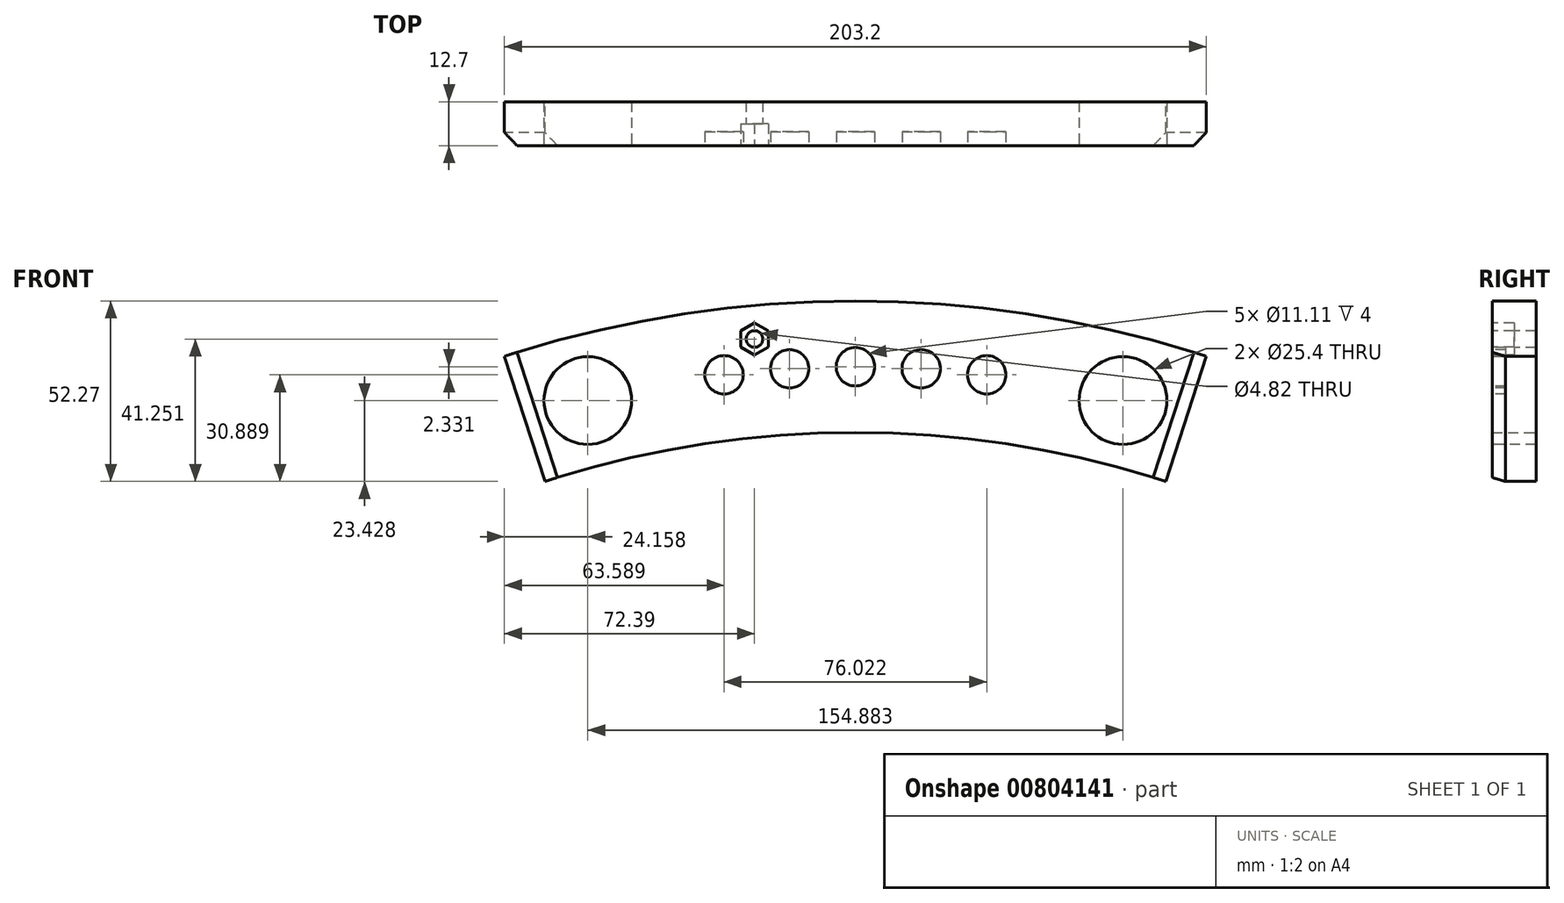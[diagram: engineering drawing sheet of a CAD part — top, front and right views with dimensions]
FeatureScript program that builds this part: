
annotation { "Feature Type Name" : "Feature", "Feature Type Description" : "" }
export const myFeature = defineFeature(function(context is Context, id is Id, definition is map)
    precondition{}
    {
        {
            var Q0;
            Q0=qCreatedBy(makeId("Front.planeOp"),FACE);
            var sketch = newSketch(context, id + "F0", { "sketchPlane" : qUnion([Q0])});
            skLineSegment(sketch, "E0", {"start": v(-101.6, 0) * mm, "end": v(101.6, 0) * mm, "construction": true});
            skArc(sketch, "E1", {"start": v(101.6, 0) * mm, "mid": v(0, 16.02) * mm, "end": v(-101.6, 0) * mm});
            skArc(sketch, "E2.0", {"start": v(89.88, -36.25) * mm, "mid": v(0, -22.08) * mm, "end": v(-89.88, -36.25) * mm});
            skLineSegment(sketch, "E3", {"start": v(-101.6, 0) * mm, "end": v(-89.88, -36.25) * mm});
            skLineSegment(sketch, "E4", {"start": v(101.6, 0) * mm, "end": v(89.88, -36.25) * mm});
            skSolve(sketch);
        }
        {
            var Q0;
            Q0 = qSketchRegion(id + "F0", true);
            extrude(context, id + "F1", {"entities" : qUnion([Q0]), "depth" : 12.7 * mm, "offsetDistance" : 25.4 * mm});
        }
        {
            var Q0;
            Q0=makeQuery(id+"F1.opExtrude","CAP_FACE",FACE,{"disambiguationData":[OSD([sQuery(id+"F0.wireOp",EDGE,"E1"),sQuery(id+"F0.wireOp",EDGE,"E2.0"),sQuery(id+"F0.wireOp",EDGE,"E3"),sQuery(id+"F0.wireOp",EDGE,"E4")])],"isStart":false});
            var sketch = newSketch(context, id + "F2", { "sketchPlane" : qUnion([Q0])});
            skLineSegment(sketch, "E5", {"start": v(0, 16.02) * mm, "end": v(0, -22.08) * mm, "construction": true});
            skPoint(sketch, "E6", {"position": v(0, -3.03) * mm});
            skArc(sketch, "E7", {"start": v(95.74, -18.13) * mm, "mid": v(0, -3.03) * mm, "end": v(-95.74, -18.13) * mm, "construction": true});
            skCircle(sketch, "E8", {"center": v(0, -3.03) * mm, "radius": 5.56 * mm});
            skCircle(sketch, "E9", {"center": v(19.04, -3.61) * mm, "radius": 5.56 * mm});
            skCircle(sketch, "E10", {"center": v(38.01, -5.36) * mm, "radius": 5.56 * mm});
            skLineSegment(sketch, "E11", {"start": v(0, -3.03) * mm, "end": v(19.04, -3.61) * mm, "construction": true});
            skLineSegment(sketch, "E12", {"start": v(19.04, -3.61) * mm, "end": v(38.01, -5.36) * mm, "construction": true});
            skCircle(sketch, "E13.MirrorC", {"center": v(-38.01, -5.36) * mm, "radius": 5.56 * mm});
            skCircle(sketch, "E14.MirrorC", {"center": v(-19.04, -3.61) * mm, "radius": 5.56 * mm});
            skSolve(sketch);
        }
        {
            var Q0;
            Q0 = qSketchRegion(id + "F2", true);
            extrude(context, id + "F3", {"entities" : qUnion([Q0]), "operationType" : NewBodyOperationType.REMOVE, "oppositeDirection" : true, "depth" : 4 * mm, "offsetDistance" : 25.4 * mm});
        }
        {
            var Q0;
            Q0=makeQuery(id+"F1.opExtrude","CAP_FACE",FACE,{"disambiguationData":[OSD([sQuery(id+"F0.wireOp",EDGE,"E1"),sQuery(id+"F0.wireOp",EDGE,"E2.0"),sQuery(id+"F0.wireOp",EDGE,"E3"),sQuery(id+"F0.wireOp",EDGE,"E4")])],"isStart":false});
            var sketch = newSketch(context, id + "F4", { "sketchPlane" : qUnion([Q0])});
            skLineSegment(sketch, "E15", {"start": v(0, 16.02) * mm, "end": v(0, -22.08) * mm, "construction": true});
            skPoint(sketch, "E16", {"position": v(0, -3.03) * mm});
            skArc(sketch, "E17", {"start": v(95.74, -18.13) * mm, "mid": v(0, -3.03) * mm, "end": v(-95.74, -18.13) * mm, "construction": true});
            skCircle(sketch, "E18", {"center": v(77.44, -12.82) * mm, "radius": 12.7 * mm});
            skCircle(sketch, "E19", {"center": v(-77.44, -12.82) * mm, "radius": 12.7 * mm});
            skLineSegment(sketch, "E20", {"start": v(77.44, -12.82) * mm, "end": v(95.74, -18.13) * mm, "construction": true});
            skLineSegment(sketch, "E21", {"start": v(-95.74, -18.13) * mm, "end": v(-77.44, -12.82) * mm, "construction": true});
            skSolve(sketch);
        }
        {
            var Q0;
            Q0 = qSketchRegion(id + "F4", true);
            extrude(context, id + "F5", {"entities" : qUnion([Q0]), "operationType" : NewBodyOperationType.REMOVE, "endBound" : BoundingType.THROUGH_ALL, "oppositeDirection" : true, "depth" : 25.4 * mm, "offsetDistance" : 25.4 * mm});
        }
        {
            var Q0;
            Q0=makeQuery(id+"F1.opExtrude","CAP_EDGE",EDGE,{"disambiguationData":[OSD([sQuery(id+"F0.wireOp",EDGE,"E3")])],"isStart":false});
            var Q1;
            Q1=makeQuery(id+"F1.opExtrude","CAP_EDGE",EDGE,{"disambiguationData":[OSD([sQuery(id+"F0.wireOp",EDGE,"E4")])],"isStart":false});
            chamfer(context, id + "F6", {"entities" : qUnion([Q0, Q1]), "width" : 3.8 * mm, "tangentPropagation" : true});
        }
        {
            var Q0;
            Q0=makeQuery(id+"F1.opExtrude","CAP_FACE",FACE,{"disambiguationData":[OSD([sQuery(id+"F0.wireOp",EDGE,"E1"),sQuery(id+"F0.wireOp",EDGE,"E2.0"),sQuery(id+"F0.wireOp",EDGE,"E3"),sQuery(id+"F0.wireOp",EDGE,"E4")])],"isStart":false});
            var sketch = newSketch(context, id + "F7", { "sketchPlane" : qUnion([Q0])});
            skCircle(sketch, "E22.cCircle", {"center": v(-29.21, 5) * mm, "radius": 4 * mm, "construction": true});
            skLineSegment(sketch, "E22.0", {"start": v(-25.2, 2.7) * mm, "end": v(-29.2, 0.38) * mm});
            skLineSegment(sketch, "E22.1", {"start": v(-29.2, 0.38) * mm, "end": v(-33.2, 2.7) * mm});
            skLineSegment(sketch, "E22.2", {"start": v(-33.2, 2.7) * mm, "end": v(-33.2, 7.31) * mm});
            skLineSegment(sketch, "E22.3", {"start": v(-33.2, 7.31) * mm, "end": v(-29.21, 9.62) * mm});
            skLineSegment(sketch, "E22.4", {"start": v(-29.2, 9.62) * mm, "end": v(-25.2, 7.31) * mm});
            skLineSegment(sketch, "E22.5", {"start": v(-25.21, 7.31) * mm, "end": v(-25.21, 2.7) * mm});
            skPoint(sketch, "E22.0.midPoint", {"position": v(-27.21, 1.54) * mm});
            skSolve(sketch);
        }
        {
            var Q0;
            Q0 = qSketchRegion(id + "F7", true);
            extrude(context, id + "F8", {"entities" : qUnion([Q0]), "operationType" : NewBodyOperationType.REMOVE, "oppositeDirection" : true, "depth" : 6.35 * mm, "offsetDistance" : 25.4 * mm});
        }
        {
            var Q0;
            Q0=makeQuery(id+"F8.boolean.opBoolean","COPY",FACE,{"derivedFrom":makeQuery(id+"F8.opExtrude","CAP_FACE",FACE,{"disambiguationData":[OSD([sQuery(id+"F7.wireOp",EDGE,"E22.0"),sQuery(id+"F7.wireOp",EDGE,"E22.1"),sQuery(id+"F7.wireOp",EDGE,"E22.2"),sQuery(id+"F7.wireOp",EDGE,"E22.3"),sQuery(id+"F7.wireOp",EDGE,"E22.4"),sQuery(id+"F7.wireOp",EDGE,"E22.5")])],"isStart":false})});
            var sketch = newSketch(context, id + "F9", { "sketchPlane" : qUnion([Q0])});
            skLineSegment(sketch, "E23.0", {"start": v(-29.2, 0.38) * mm, "end": v(-33.2, 2.7) * mm, "construction": true});
            skLineSegment(sketch, "E23.1", {"start": v(-25.2, 2.7) * mm, "end": v(-29.2, 0.38) * mm, "construction": true});
            skLineSegment(sketch, "E23.2", {"start": v(-25.21, 7.31) * mm, "end": v(-25.21, 2.7) * mm, "construction": true});
            skLineSegment(sketch, "E23.3", {"start": v(-29.2, 9.62) * mm, "end": v(-25.2, 7.31) * mm, "construction": true});
            skLineSegment(sketch, "E23.4", {"start": v(-33.2, 7.31) * mm, "end": v(-29.21, 9.62) * mm, "construction": true});
            skLineSegment(sketch, "E23.5", {"start": v(-33.2, 2.7) * mm, "end": v(-33.2, 7.31) * mm, "construction": true});
            skLineSegment(sketch, "E24", {"start": v(-29.2, 9.62) * mm, "end": v(-29.2, 0.38) * mm, "construction": true});
            skLineSegment(sketch, "E25", {"start": v(-25.21, 5) * mm, "end": v(-33.2, 5) * mm, "construction": true});
            skCircle(sketch, "E26", {"center": v(-29.2, 5) * mm, "radius": 2.4 * mm});
            skSolve(sketch);
        }
        {
            var Q0;
            Q0 = qSketchRegion(id + "F9", true);
            extrude(context, id + "F10", {"entities" : qUnion([Q0]), "operationType" : NewBodyOperationType.REMOVE, "endBound" : BoundingType.THROUGH_ALL, "oppositeDirection" : true, "depth" : 25.4 * mm, "offsetDistance" : 25.4 * mm});
        }
    });
